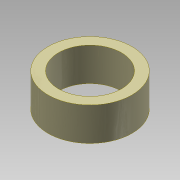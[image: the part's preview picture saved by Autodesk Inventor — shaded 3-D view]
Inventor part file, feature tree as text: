
AUTODESK INVENTOR PART (.ipt)
format: ipt  version: 2013 SP2 (Build 170200200, 200)  size: 79,360 bytes
history: native  units: mm
features: extrude x1, sketch x1
ambient origin geometry x8: Origin, YZ Plane, XZ Plane, XY Plane, X Axis, Y Axis, Z Axis, Center Point
bodies: Solid1 (feature_tree)
feature tree (2):
  extrude  "Extrusion1"  Depth=8.0mm
  sketch  "Sketch1"  dims[d0=6.0mm d1=8.0mm d2=3.175mm d3=0.0mm]
